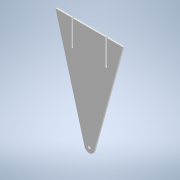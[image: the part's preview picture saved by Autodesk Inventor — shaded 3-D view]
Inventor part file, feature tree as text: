
AUTODESK INVENTOR PART (.ipt)
format: ipt  version: 2022 (Build 260153000, 153)  size: 117,760 bytes
history: native  units: mm
features: other x3, extrude x1, sketch x1, reference x1
ambient origin geometry x8: Origin, YZ Plane, XZ Plane, XY Plane, X Axis, Y Axis, Z Axis, Center Point
bodies: Body1 (feature_tree)
feature tree (6):
  extrude  "Extrusion2"  Depth=65.0mm
  sketch  "Sketch1"  dims[d0=200.0mm d1=65.0mm d2=19.0mm d7=50.0mm d8=3.0mm d9=31.0mm d10=1.5mm d11=1.5mm d12=0.0mm d13=0.0mm]
  reference  "Reference1"
  other  "<userpath>\OneDrive\Escritorio\Mini_Proyecto_Diseno\Diseno_18012\Modelo_MPD\Carril.iam"
  other  "Carril.iam"
  other  "Sujetador_Carril:1"
